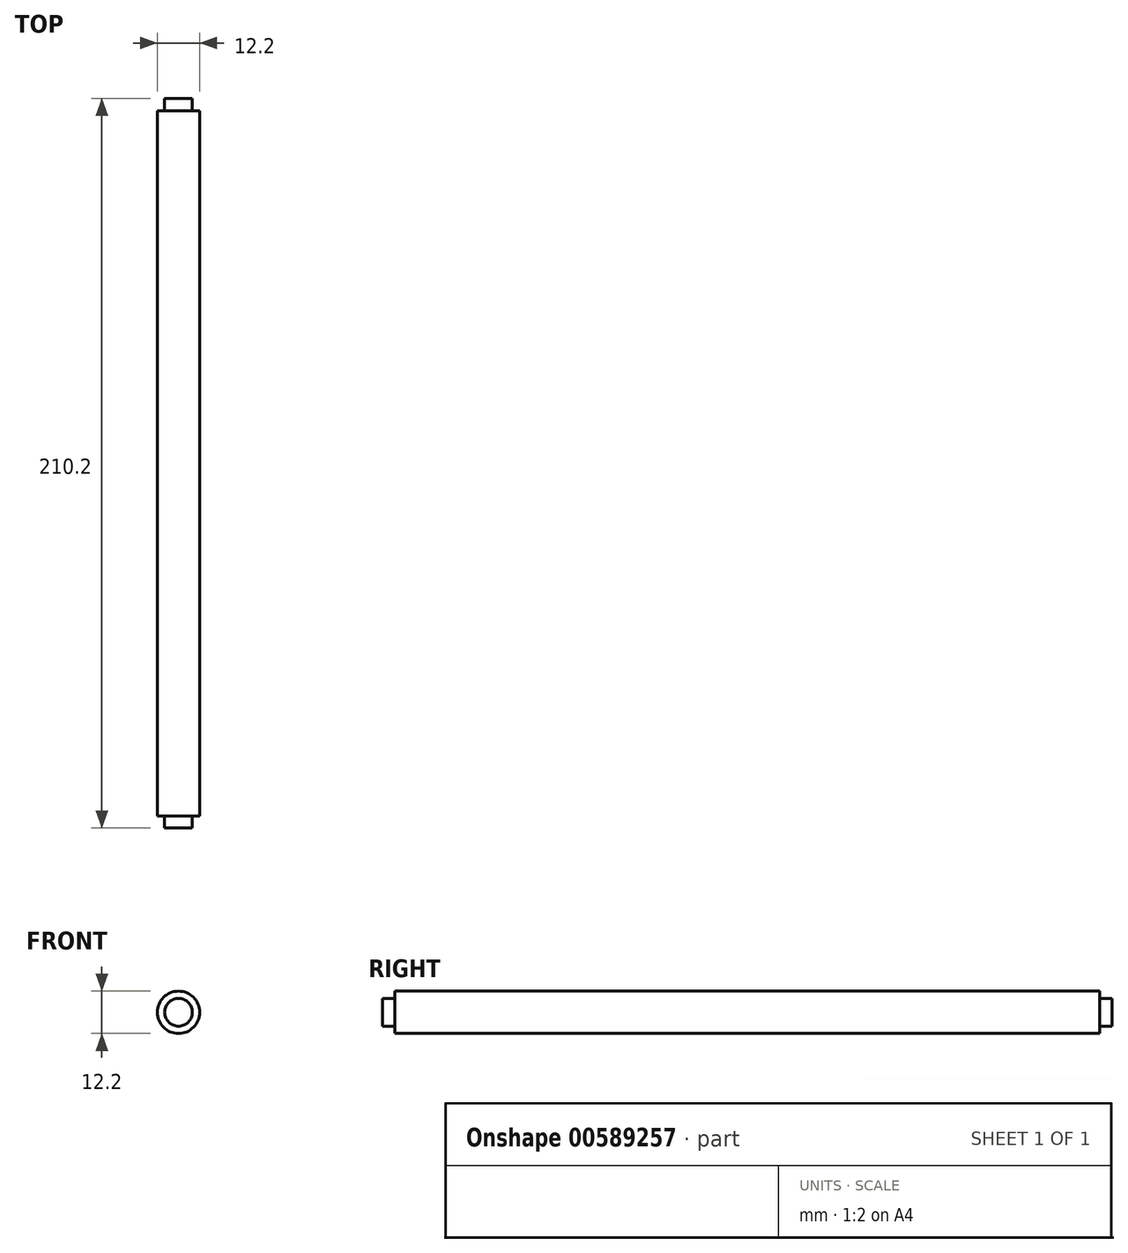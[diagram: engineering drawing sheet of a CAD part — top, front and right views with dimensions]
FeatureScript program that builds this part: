
annotation { "Feature Type Name" : "Feature", "Feature Type Description" : "" }
export const myFeature = defineFeature(function(context is Context, id is Id, definition is map)
    precondition{}
    {
        {
            var Q0;
            Q0=qCreatedBy(makeId("Front.planeOp"),FACE);
            var sketch = newSketch(context, id + "F0", { "sketchPlane" : qUnion([Q0])});
            skCircle(sketch, "E0", {"center": v(0, 0) * mm, "radius": 6.1 * mm});
            skCircle(sketch, "E1", {"center": v(0, 0) * mm, "radius": 4 * mm});
            skSolve(sketch);
        }
        {
            var Q0;
            Q0=makeQuery(id+"F0.imprint","IMPRINT",FACE,{"disambiguationData":[TD([[makeQuery(id+"F0.imprint","IMPRINT",EDGE,{"derivedFrom":sQuery(id+"F0.wireOp",EDGE,"E0")}),1.0]])]});
            extrude(context, id + "F1", {"entities" : qUnion([Q0]), "endBound" : BoundingType.SYMMETRIC, "depth" : (8 * 25.4) * mm, "offsetDistance" : 25 * mm});
        }
        {
            var Q0;
            Q0=makeQuery(id+"F0.imprint","IMPRINT",FACE,{"disambiguationData":[TD([[makeQuery(id+"F0.imprint","IMPRINT",EDGE,{"derivedFrom":sQuery(id+"F0.wireOp",EDGE,"E1")}),1.0]])]});
            extrude(context, id + "F2", {"entities" : qUnion([Q0]), "operationType" : NewBodyOperationType.ADD, "endBound" : BoundingType.SYMMETRIC, "depth" : ((8 * 25.4) + 7) * mm, "offsetDistance" : 25 * mm});
        }
        {
            var Q0;
            Q0=qCreatedBy(makeId("Top.planeOp"),FACE);
            cPlane(context, id + "F3", {"entities" : qUnion([Q0]), "cplaneType" : CPlaneType.OFFSET, "offset" : (.240 * 25.4) * mm, "width" : 150 * mm, "height" : 150 * mm});
        }
        {
            var Q0;
            Q0=qCreatedBy(id+"F3.planeOp",FACE);
            var sketch = newSketch(context, id + "F4", { "sketchPlane" : qUnion([Q0])});
            skPoint(sketch, "E2", {"position": v(0, 0) * mm});
            skSolve(sketch);
        }
    });
